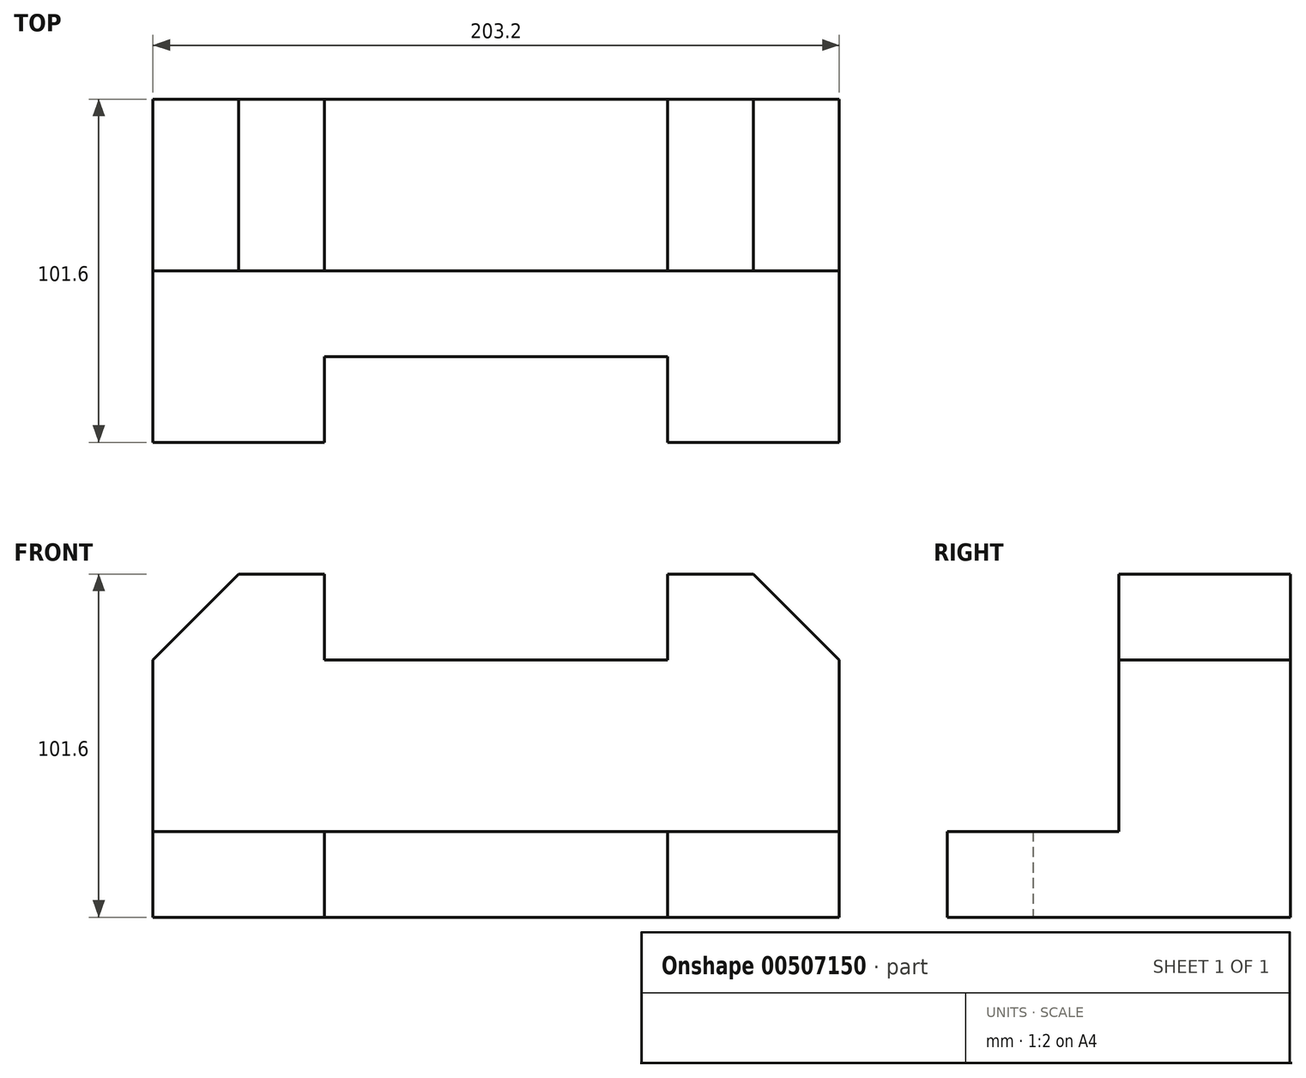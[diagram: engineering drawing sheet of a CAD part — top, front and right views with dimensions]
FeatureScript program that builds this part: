
annotation { "Feature Type Name" : "Feature", "Feature Type Description" : "" }
export const myFeature = defineFeature(function(context is Context, id is Id, definition is map)
    precondition{}
    {
        {
            var Q0;
            Q0=qCreatedBy(makeId("Front.planeOp"),FACE);
            var sketch = newSketch(context, id + "F0", { "sketchPlane" : qUnion([Q0])});
            skLineSegment(sketch, "E0.bottom", {"start": v(3.04, 0) * mm, "end": v(-200.16, 0) * mm});
            skLineSegment(sketch, "E0.top", {"start": v(3.04, 25.4) * mm, "end": v(-200.16, 25.4) * mm});
            skLineSegment(sketch, "E0.left", {"start": v(3.04, 0) * mm, "end": v(3.04, 25.4) * mm});
            skLineSegment(sketch, "E0.right", {"start": v(-200.16, 0) * mm, "end": v(-200.16, 25.4) * mm});
            skSolve(sketch);
        }
        {
            var Q0;
            Q0=makeQuery(id+"F0.imprint","IMPRINT",FACE,{"disambiguationData":[TD([[makeQuery(id+"F0.imprint","IMPRINT",EDGE,{"derivedFrom":sQuery(id+"F0.wireOp",EDGE,"E0.bottom")}),-1.0]])]});
            extrude(context, id + "F1", {"entities" : qUnion([Q0]), "depth" : 101.6 * mm});
        }
        {
            var Q0;
            Q0=makeQuery(id+"F1.opExtrude","CAP_FACE",FACE,{"disambiguationData":[OSD([sQuery(id+"F0.wireOp",EDGE,"E0.bottom"),sQuery(id+"F0.wireOp",EDGE,"E0.top"),sQuery(id+"F0.wireOp",EDGE,"E0.left"),sQuery(id+"F0.wireOp",EDGE,"E0.right")])],"isStart":false});
            var sketch = newSketch(context, id + "F2", { "sketchPlane" : qUnion([Q0])});
            skLineSegment(sketch, "E1.bottom", {"start": v(-149.36, 25.4) * mm, "end": v(-47.76, 25.4) * mm});
            skLineSegment(sketch, "E1.top", {"start": v(-149.36, 0) * mm, "end": v(-47.76, 0) * mm});
            skLineSegment(sketch, "E1.left", {"start": v(-149.36, 25.4) * mm, "end": v(-149.36, 0) * mm});
            skLineSegment(sketch, "E1.right", {"start": v(-47.76, 25.4) * mm, "end": v(-47.76, 0) * mm});
            skLineSegment(sketch, "E2.bottom", {"start": v(-149.36, 0) * mm, "end": v(-200.16, 0) * mm});
            skLineSegment(sketch, "E2.top", {"start": v(-149.36, 0) * mm, "end": v(-200.16, 0) * mm});
            skLineSegment(sketch, "E2.left", {"start": v(-149.36, 0) * mm, "end": v(-149.36, 0) * mm});
            skLineSegment(sketch, "E2.right", {"start": v(-200.16, 0) * mm, "end": v(-200.16, 0) * mm});
            skSolve(sketch);
        }
        {
            var Q0;
            Q0=makeQuery(id+"F2.imprint","IMPRINT",FACE,{"disambiguationData":[TD([[makeQuery(id+"F2.imprint","IMPRINT",EDGE,{"derivedFrom":sQuery(id+"F2.wireOp",EDGE,"E1.bottom")}),1.0]])]});
            extrude(context, id + "F3", {"entities" : qUnion([Q0]), "operationType" : NewBodyOperationType.REMOVE, "oppositeDirection" : true, "depth" : 25.4 * mm});
        }
        {
            var Q0;
            Q0=makeQuery(id+"F1.opExtrude","SWEPT_FACE",FACE,{"disambiguationData":[OSD([sQuery(id+"F0.wireOp",EDGE,"E0.left")])]});
            var sketch = newSketch(context, id + "F4", { "sketchPlane" : qUnion([Q0])});
            skLineSegment(sketch, "E3.bottom", {"start": v(0, 25.4) * mm, "end": v(-50.8, 25.4) * mm});
            skLineSegment(sketch, "E3.top", {"start": v(0, 76.2) * mm, "end": v(-50.8, 76.2) * mm});
            skLineSegment(sketch, "E3.left", {"start": v(0, 25.4) * mm, "end": v(0, 76.2) * mm});
            skLineSegment(sketch, "E3.right", {"start": v(-50.8, 25.4) * mm, "end": v(-50.8, 76.2) * mm});
            skSolve(sketch);
        }
        {
            var Q0;
            Q0=makeQuery(id+"F4.imprint","IMPRINT",FACE,{"disambiguationData":[TD([[makeQuery(id+"F4.imprint","IMPRINT",EDGE,{"derivedFrom":sQuery(id+"F4.wireOp",EDGE,"E3.bottom")}),1.0]])]});
            extrude(context, id + "F5", {"entities" : qUnion([Q0]), "operationType" : NewBodyOperationType.ADD, "oppositeDirection" : true, "depth" : 203.2 * mm});
        }
        {
            var Q0;
            Q0=makeQuery(id+"F5.boolean.opBoolean","MERGE",FACE,{"derivedFrom":[makeQuery(id+"F1.opExtrude","CAP_FACE",FACE,{"disambiguationData":[OSD([sQuery(id+"F0.wireOp",EDGE,"E0.bottom"),sQuery(id+"F0.wireOp",EDGE,"E0.top"),sQuery(id+"F0.wireOp",EDGE,"E0.left"),sQuery(id+"F0.wireOp",EDGE,"E0.right")])],"isStart":true}),makeQuery(id+"F5.opExtrude","SWEPT_FACE",FACE,{"disambiguationData":[OSD([sQuery(id+"F4.wireOp",EDGE,"E3.left")])]})]});
            var sketch = newSketch(context, id + "F6", { "sketchPlane" : qUnion([Q0])});
            skLineSegment(sketch, "E4", {"start": v(-3.04, 76.2) * mm, "end": v(22.36, 101.6) * mm});
            skLineSegment(sketch, "E5", {"start": v(22.36, 101.6) * mm, "end": v(47.76, 101.6) * mm});
            skLineSegment(sketch, "E6", {"start": v(47.76, 101.6) * mm, "end": v(47.76, 76.2) * mm});
            skLineSegment(sketch, "E7", {"start": v(47.76, 76.2) * mm, "end": v(-3.04, 76.2) * mm});
            skSolve(sketch);
        }
        {
            var Q0;
            Q0=makeQuery(id+"F6.imprint","IMPRINT",FACE,{"disambiguationData":[TD([[makeQuery(id+"F6.imprint","IMPRINT",EDGE,{"derivedFrom":sQuery(id+"F6.wireOp",EDGE,"E4")}),-1.0]])]});
            extrude(context, id + "F7", {"entities" : qUnion([Q0]), "operationType" : NewBodyOperationType.ADD, "oppositeDirection" : true, "depth" : 50.8 * mm});
        }
        {
            var Q0;
            Q0=makeQuery(id+"F7.boolean.opBoolean","MERGE",FACE,{"derivedFrom":[makeQuery(id+"F5.boolean.opBoolean","MERGE",FACE,{"derivedFrom":[makeQuery(id+"F1.opExtrude","CAP_FACE",FACE,{"disambiguationData":[OSD([sQuery(id+"F0.wireOp",EDGE,"E0.bottom"),sQuery(id+"F0.wireOp",EDGE,"E0.top"),sQuery(id+"F0.wireOp",EDGE,"E0.left"),sQuery(id+"F0.wireOp",EDGE,"E0.right")])],"isStart":true}),makeQuery(id+"F5.opExtrude","SWEPT_FACE",FACE,{"disambiguationData":[OSD([sQuery(id+"F4.wireOp",EDGE,"E3.left")])]})]}),makeQuery(id+"F7.opExtrude","CAP_FACE",FACE,{"disambiguationData":[OSD([sQuery(id+"F6.wireOp",EDGE,"E4"),sQuery(id+"F6.wireOp",EDGE,"E5"),sQuery(id+"F6.wireOp",EDGE,"E6"),sQuery(id+"F6.wireOp",EDGE,"E7")])],"isStart":true})]});
            var sketch = newSketch(context, id + "F8", { "sketchPlane" : qUnion([Q0])});
            skLineSegment(sketch, "E8", {"start": v(200.16, 76.2) * mm, "end": v(174.76, 101.6) * mm});
            skLineSegment(sketch, "E9", {"start": v(174.76, 101.6) * mm, "end": v(149.36, 101.6) * mm});
            skLineSegment(sketch, "E10", {"start": v(149.36, 101.6) * mm, "end": v(149.36, 76.2) * mm});
            skLineSegment(sketch, "E11", {"start": v(149.36, 76.2) * mm, "end": v(200.16, 76.2) * mm});
            skSolve(sketch);
        }
        {
            var Q0;
            Q0=makeQuery(id+"F8.imprint","IMPRINT",FACE,{"disambiguationData":[TD([[makeQuery(id+"F8.imprint","IMPRINT",EDGE,{"derivedFrom":sQuery(id+"F8.wireOp",EDGE,"E8")}),1.0]])]});
            extrude(context, id + "F9", {"entities" : qUnion([Q0]), "operationType" : NewBodyOperationType.ADD, "oppositeDirection" : true, "depth" : 50.8 * mm});
        }
    });
